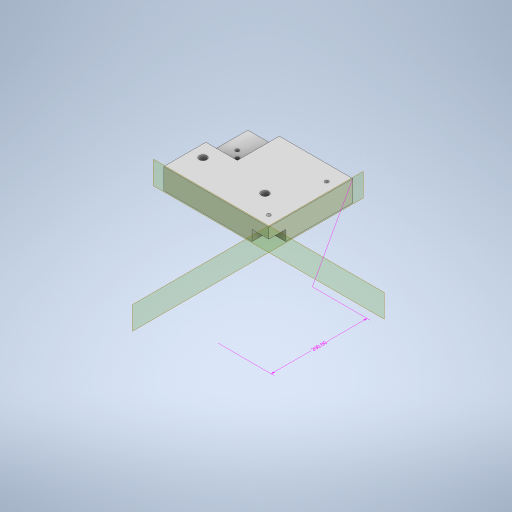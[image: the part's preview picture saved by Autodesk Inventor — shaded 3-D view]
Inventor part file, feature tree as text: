
AUTODESK INVENTOR PART (.ipt)
format: ipt  version: 2023 (Build 270158000, 158)  size: 431,616 bytes
history: native  units: mm
features: sketch x10, extrude x5, hole x5, other x3, plane x2, split x2
ambient origin geometry x8: Origin, YZ Plane, XZ Plane, XY Plane, X Axis, Y Axis, Z Axis, Center Point
bodies: Body1 (feature_tree)
feature tree (27):
  other  "Sólido1"
  other  "Anotaciones"
  extrude  "Extrusión1"  Depth=160.0mm
  extrude  "Extrusión2"  Depth=30.0mm
  hole  "Agujero1"  [1 undecoded]
  extrude  "Extrusión3"  Depth=11.75mm
  hole  "Agujero2"  [1 undecoded]
  hole  "Agujero3"  [1 undecoded]
  extrude  "Extrusión4"  TaperAngle=0.0deg  [1 undecoded]
  plane  "Plano de trabajo1"
  plane  "Plano de trabajo2"
  hole  "Agujero4"  [1 undecoded]
  hole  "Agujero5"  [1 undecoded]
  extrude  "Extrusión5"  Depth=70.0mm
  split  "Dividir1"
  split  "Dividir2"
  sketch  "Boceto1"  dims[d0=200.0mm d1=160.0mm]
  sketch  "Boceto2"  dims[d2=20.0mm d3=0.0mm d4=30.0mm]
  sketch  "Boceto3"  dims[d5=40.0mm d6=10.0mm d7=0.0mm]
  sketch  "Boceto4"  dims[d23=21.75mm d24=11.75mm]
  sketch  "Boceto5"  dims[d26=11.75mm]
  sketch  "Boceto6"  dims[d27=3.5mm d28=6.0mm d29=4.0mm d30=2.0mm d31=90.0deg d32=8.0mm d33=20.594885mm d34=30.0mm]
  sketch  "Boceto7"  dims[d35=10.0mm d36=30.0mm]
  sketch  "Boceto8"  dims[d37=40.0mm d38=0.0mm]
  sketch  "Boceto9"  dims[d39=10.0mm d40=10.0mm d41=40.0mm d42=0.0mm d43=6.5mm d44=6.5mm d45=3.5mm d46=3.5mm d47=11.749873mm d48=11.75mm d49=0.0mm]
  sketch  "Boceto10"  dims[d50=11.75mm d51=0.0mm d52=3.5mm d53=6.0mm d54=4.0mm d55=2.0mm d56=90.0deg d57=8.0mm d58=20.594885mm d59=7.0mm d60=7.0mm d61=7.0mm d62=39.0mm d63=46.0mm d64=59.0mm d65=46.0mm d66=39.0mm d67=59.0mm d68=52.0mm d69=70.0mm d70=22.0mm d71=42.0mm d72=3.5mm d73=3.5mm d74=3.5mm d75=3.5mm d76=3.5mm d77=6.0mm d78=4.0mm d79=2.0mm d80=90.0deg d81=8.0mm d82=20.594885mm d83=7.0mm d84=7.0mm d85=7.0mm d86=39.0mm d87=46.0mm d88=59.0mm d89=46.0mm d90=39.0mm d91=59.0mm d92=20.0mm d93=0.0mm d97=40.000127mm d98=10.0mm d99=30.0mm d100=10.0mm d101=5.0mm d102=5.0mm d103=5.0mm d104=5.0mm d105=45.0deg d106=45.0deg d107=10.0mm d108=10.0mm d109=30.0mm d110=5.0mm d111=5.0mm d112=5.0mm d113=5.0mm d114=10.0mm d115=30.0mm d116=5.0mm d117=5.0mm d118=5.0mm d119=5.0mm d120=10.0mm d121=3.5mm d122=6.0mm d123=4.0mm d124=2.0mm d125=90.0deg d126=8.0mm d127=20.594885mm d128=3.5mm d129=10.0mm d130=10.0mm d131=3.5mm d132=6.0mm d133=4.0mm d134=2.0mm d135=90.0deg d136=8.0mm d137=20.594885mm d138=32.0mm d139=32.0mm d140=10.0mm d141=0.0mm d142=17.37633mm d143=12.709242mm d144=6.683722mm d145=12.708891mm d146=5.220756mm d147=1.603663mm d148=2.153068mm d149=6.490327mm d94=6.100674mm d95=2.550465mm d96=200.0mm]
  other  "Cota lineal 1"
note: 6 required parameter values undecoded (feature->parameter linkage not recoverable at this tier; creation-order binding heuristic only, values carry confidence <= 0.55)
